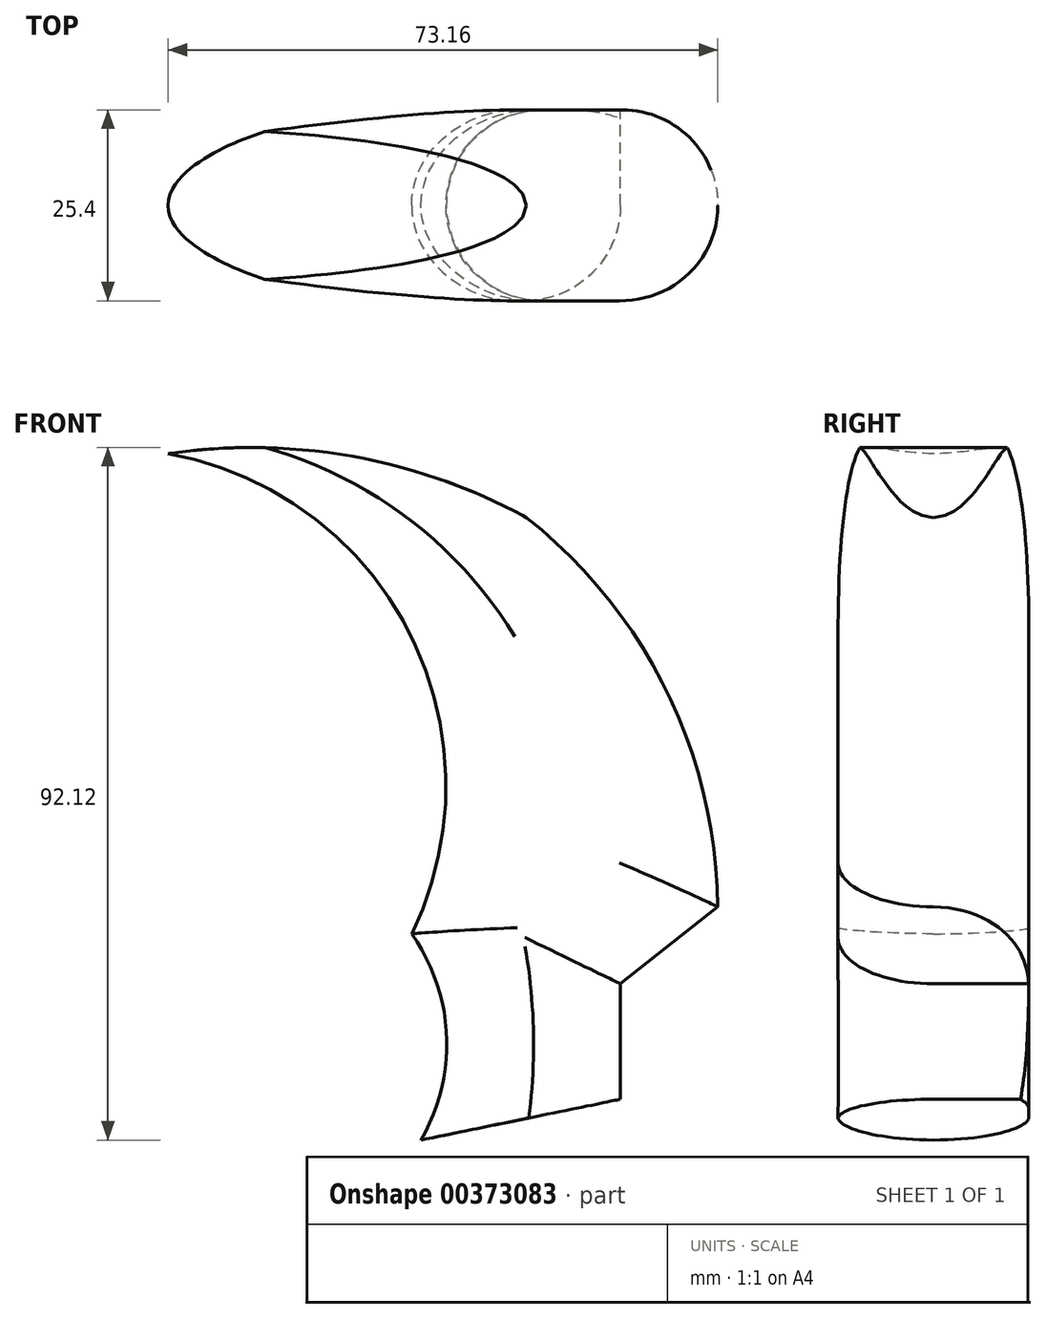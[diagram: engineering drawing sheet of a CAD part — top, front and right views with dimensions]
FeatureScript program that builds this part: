
annotation { "Feature Type Name" : "Feature", "Feature Type Description" : "" }
export const myFeature = defineFeature(function(context is Context, id is Id, definition is map)
    precondition{}
    {
        {
            var Q0;
            Q0=qCreatedBy(makeId("Front.planeOp"),FACE);
            var sketch = newSketch(context, id + "F0", { "sketchPlane" : qUnion([Q0])});
            skLineSegment(sketch, "E0", {"start": v(-4.15, 21.27) * mm, "end": v(-15.25, 27.44) * mm});
            skArc(sketch, "E1", {"start": v(-15.25, 27.44) * mm, "mid": v(-15.55, 67.45) * mm, "end": v(-47.67, 91.3) * mm});
            skArc(sketch, "E2", {"start": v(25.5, 31.02) * mm, "mid": v(18.63, 59.8) * mm, "end": v(0, 82.8) * mm});
            skArc(sketch, "E3", {"start": v(0, 82.8) * mm, "mid": v(-23.14, 90.94) * mm, "end": v(-47.67, 91.3) * mm});
            skArc(sketch, "E4", {"start": v(-14.02, 0) * mm, "mid": v(-10.6, 13.9) * mm, "end": v(-15.25, 27.44) * mm});
            skLineSegment(sketch, "E5", {"start": v(12.53, 20.78) * mm, "end": v(25.5, 31.02) * mm});
            skCircle(sketch, "E6", {"center": v(0, -41.35) * mm, "radius": 3.18 * mm});
            skLineSegment(sketch, "E7", {"start": v(12.53, 20.78) * mm, "end": v(12.53, 5.43) * mm});
            skLineSegment(sketch, "E8", {"start": v(12.53, 5.43) * mm, "end": v(-14.02, 0) * mm});
            skSolve(sketch);
        }
        {
            var Q0;
            Q0=makeQuery(id+"F0.imprint","IMPRINT",FACE,{"disambiguationData":[TD([[makeQuery(id+"F0.imprint","IMPRINT",EDGE,{"derivedFrom":sQuery(id+"F0.wireOp",EDGE,"E1")}),-1.0]])]});
            extrude(context, id + "F1", {"entities" : qUnion([Q0]), "depth" : 25.4 * mm});
        }
        {
            var Q0;
            Q0=makeQuery(id+"F1.opExtrude","CAP_EDGE",EDGE,{"disambiguationData":[OSD([sQuery(id+"F0.wireOp",EDGE,"E1")])],"isStart":false});
            var Q1;
            Q1=makeQuery(id+"F1.opExtrude","CAP_EDGE",EDGE,{"disambiguationData":[OSD([sQuery(id+"F0.wireOp",EDGE,"E1")])],"isStart":true});
            var Q2;
            Q2=makeQuery(id+"F1.opExtrude","CAP_EDGE",EDGE,{"disambiguationData":[OSD([sQuery(id+"F0.wireOp",EDGE,"E2")])],"isStart":true});
            var Q3;
            Q3=makeQuery(id+"F1.opExtrude","CAP_EDGE",EDGE,{"disambiguationData":[OSD([sQuery(id+"F0.wireOp",EDGE,"E2")])],"isStart":false});
            var Q4;
            Q4=makeQuery(id+"F1.opExtrude","CAP_EDGE",EDGE,{"disambiguationData":[OSD([sQuery(id+"F0.wireOp",EDGE,"E3")])],"isStart":false});
            var Q5;
            Q5=makeQuery(id+"F1.opExtrude","CAP_EDGE",EDGE,{"disambiguationData":[OSD([sQuery(id+"F0.wireOp",EDGE,"E3")])],"isStart":true});
            var Q6;
            Q6=makeQuery(id+"F1.opExtrude","CAP_EDGE",EDGE,{"disambiguationData":[OSD([sQuery(id+"F0.wireOp",EDGE,"E4")])],"isStart":false});
            var Q7;
            Q7=makeQuery(id+"F1.opExtrude","CAP_EDGE",EDGE,{"disambiguationData":[OSD([sQuery(id+"F0.wireOp",EDGE,"lIkkYURh-w8zZ-dkGo-bhBr-hgc90XVFGhCK")])],"isStart":false});
            var Q8;
            Q8=makeQuery(id+"F1.opExtrude","CAP_FACE",FACE,{"disambiguationData":[OSD([sQuery(id+"F0.wireOp",EDGE,"E1"),sQuery(id+"F0.wireOp",EDGE,"E2"),sQuery(id+"F0.wireOp",EDGE,"E3"),sQuery(id+"F0.wireOp",EDGE,"OCtpaNLE-z2dQ-zv6v-IivT-vU28FLkQa9g1"),sQuery(id+"F0.wireOp",EDGE,"E4"),sQuery(id+"F0.wireOp",EDGE,"lIkkYURh-w8zZ-dkGo-bhBr-hgc90XVFGhCK"),sQuery(id+"F0.wireOp",EDGE,"t47hnsBS-8Hg5-5wQN-69gc-sVCeoA08l0ob"),sQuery(id+"F0.wireOp",EDGE,"E5"),sQuery(id+"F0.wireOp",EDGE,"E6"),sQuery(id+"F0.wireOp",EDGE,"vVZ8OzRF-CYv3-wDfl-k6jL-hm1CFqalxQ6A")])],"isStart":false});
            var Q9;
            Q9=makeQuery(id+"F1.opExtrude","CAP_EDGE",EDGE,{"disambiguationData":[OSD([sQuery(id+"F0.wireOp",EDGE,"E4")])],"isStart":true});
            var Q10;
            Q10=makeQuery(id+"F1.opExtrude","CAP_EDGE",EDGE,{"disambiguationData":[OSD([sQuery(id+"F0.wireOp",EDGE,"lIkkYURh-w8zZ-dkGo-bhBr-hgc90XVFGhCK")])],"isStart":true});
            var Q11;
            Q11=makeQuery(id+"F1.opExtrude","CAP_EDGE",EDGE,{"disambiguationData":[OSD([sQuery(id+"F0.wireOp",EDGE,"t47hnsBS-8Hg5-5wQN-69gc-sVCeoA08l0ob")])],"isStart":true});
            var Q12;
            Q12=makeQuery(id+"F1.opExtrude","CAP_EDGE",EDGE,{"disambiguationData":[OSD([sQuery(id+"F0.wireOp",EDGE,"OCtpaNLE-z2dQ-zv6v-IivT-vU28FLkQa9g1")])],"isStart":true});
            var Q13;
            Q13=makeQuery(id+"F1.opExtrude","CAP_EDGE",EDGE,{"disambiguationData":[OSD([sQuery(id+"F0.wireOp",EDGE,"OCtpaNLE-z2dQ-zv6v-IivT-vU28FLkQa9g1")])],"isStart":false});
            fillet(context, id + "F2", {"entities" : qUnion([Q0, Q1, Q2, Q3, Q4, Q5, Q6, Q7, Q8, Q9, Q10, Q11, Q12, Q13]), "radius" : 12.7 * mm, "tangentPropagation" : true, "allowEdgeOverflow" : false});
        }
    });
